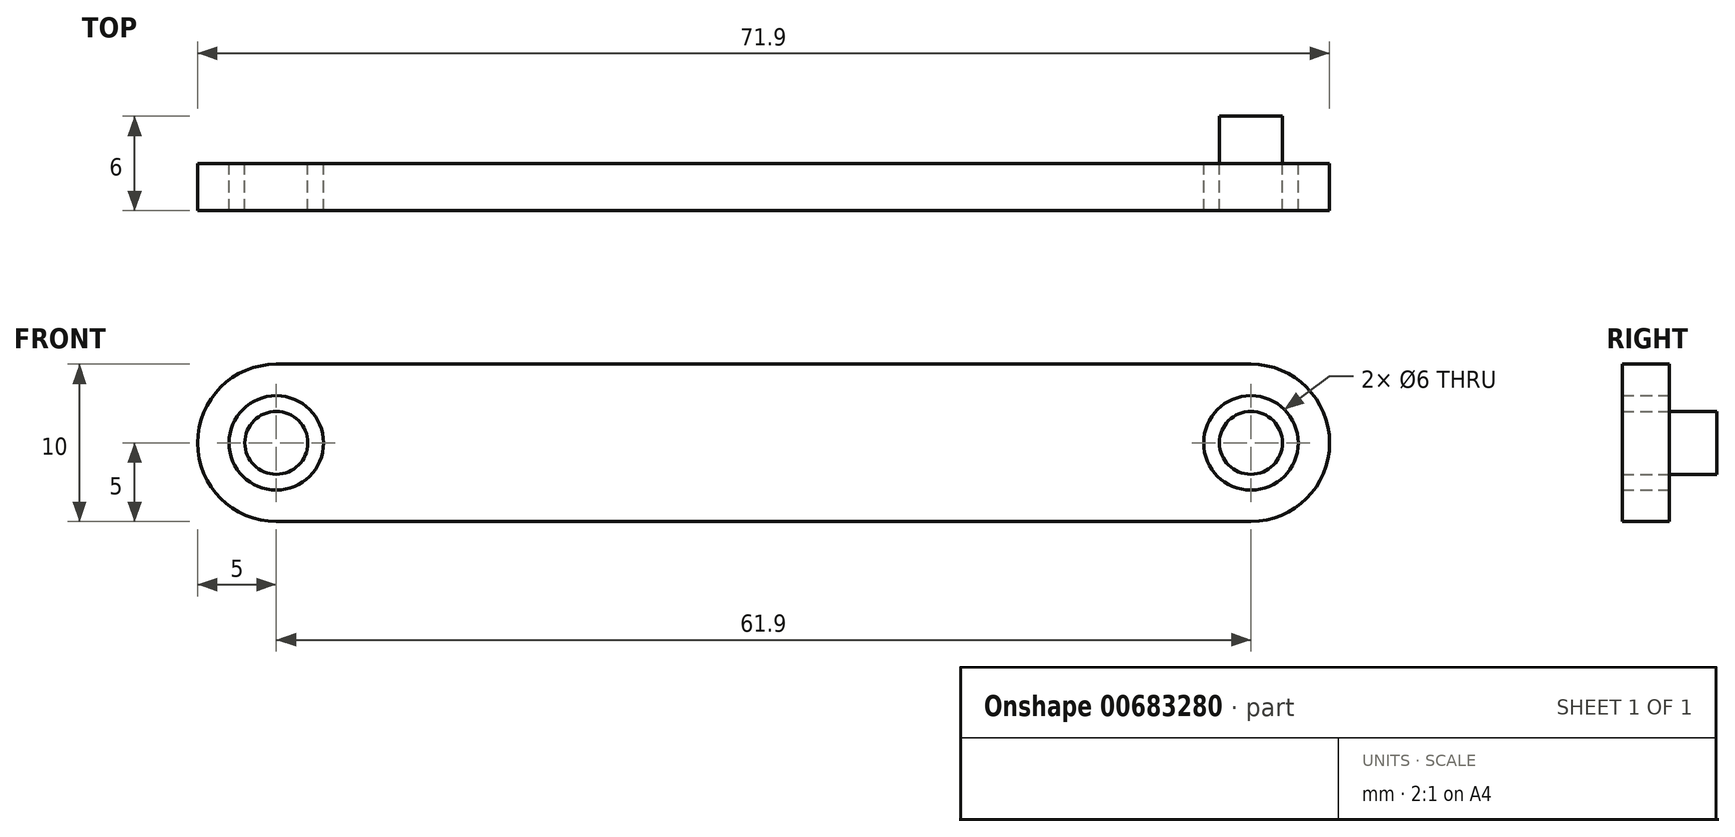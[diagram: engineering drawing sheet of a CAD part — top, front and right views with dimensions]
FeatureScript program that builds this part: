
annotation { "Feature Type Name" : "Feature", "Feature Type Description" : "" }
export const myFeature = defineFeature(function(context is Context, id is Id, definition is map)
    precondition{}
    {
        {
            var Q0;
            Q0=qCreatedBy(makeId("Front.planeOp"),FACE);
            var sketch = newSketch(context, id + "F0", { "sketchPlane" : qUnion([Q0])});
            skArc(sketch, "E0", {"start": v(-30.95, 5) * mm, "mid": v(-35.95, 0) * mm, "end": v(-30.95, -5) * mm});
            skArc(sketch, "E1", {"start": v(30.95, -5) * mm, "mid": v(35.95, 0) * mm, "end": v(30.95, 5) * mm});
            skCircle(sketch, "E2", {"center": v(-30.95, 0) * mm, "radius": 3 * mm});
            skCircle(sketch, "E3", {"center": v(-30.95, 0) * mm, "radius": 2 * mm});
            skCircle(sketch, "E4", {"center": v(30.95, 0) * mm, "radius": 3 * mm});
            skCircle(sketch, "E5", {"center": v(30.95, 0) * mm, "radius": 2 * mm});
            skLineSegment(sketch, "E6", {"start": v(-30.95, 5) * mm, "end": v(30.95, 5) * mm});
            skLineSegment(sketch, "E7", {"start": v(-30.95, -5) * mm, "end": v(30.95, -5) * mm});
            skSolve(sketch);
        }
        {
            var Q0;
            Q0 = qSketchRegion(id + "F0", true);
            var Q1;
            Q1=makeQuery(id+"F0.imprint","IMPRINT",FACE,{"disambiguationData":[TD([[makeQuery(id+"F0.imprint","IMPRINT",EDGE,{"derivedFrom":sQuery(id+"F0.wireOp",EDGE,"E3")}),1.0]])]});
            var Q2;
            Q2=makeQuery(id+"F0.imprint","IMPRINT",FACE,{"disambiguationData":[TD([[makeQuery(id+"F0.imprint","IMPRINT",EDGE,{"derivedFrom":sQuery(id+"F0.wireOp",EDGE,"E5")}),1.0]])]});
            extrude(context, id + "F1", {"entities" : qUnion([Q0, Q1, Q2]), "depth" : 3 * mm, "offsetDistance" : 25 * mm});
        }
        {
            var Q0;
            Q0=makeQuery(id+"F1.opExtrude","CAP_FACE",FACE,{"disambiguationData":[OSD([sQuery(id+"F0.wireOp",EDGE,"E5")])],"isStart":true});
            extrude(context, id + "F2", {"entities" : qUnion([Q0]), "operationType" : NewBodyOperationType.ADD, "depth" : 3 * mm, "offsetDistance" : 25 * mm});
        }
    });
